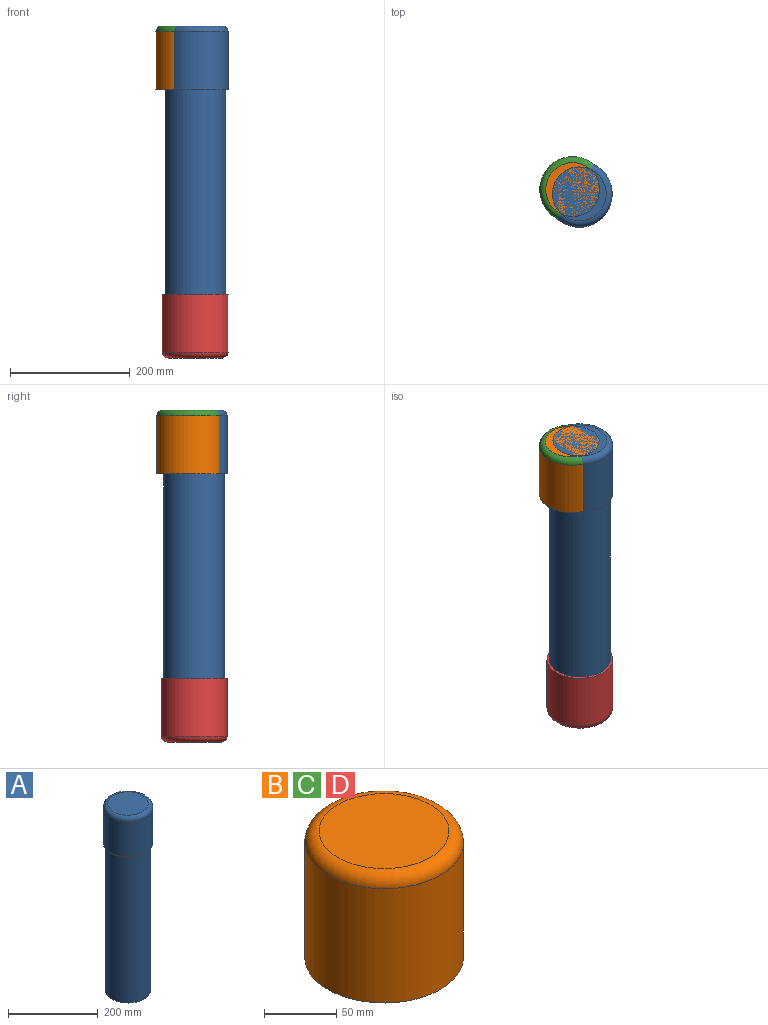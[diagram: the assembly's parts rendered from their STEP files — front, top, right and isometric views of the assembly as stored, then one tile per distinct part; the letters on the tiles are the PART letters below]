
ASSEMBLY  parts=4 mates=1
PART A: 8 faces, bbox 119.1x119.1x507 mm
  f0: cylinder r=46mm len=500mm, axis (0,0,1), area 144513.3mm2, adj f2,f3
  f1: cylinder r=51mm len=400mm, axis (0,0,1), area 128177mm2, adj f2,f4
  f2: plane 102x102mm, normal (0,0,-1), area 1523.7mm2, adj f0,f1
  f3: plane 92x92mm, normal (0,0,-1), area 6647.6mm2, adj f0
  f4: plane 110x110mm, normal (0,0,-1), area 1332mm2, adj f1,f6
  f5: plane 90x90mm, normal (0,0,1), area 6361.7mm2, adj f7
  f6: cylinder r=55mm len=110mm, axis (0,0,-1), area 33520.8mm2, adj f4,f7
  f7: torus R=45mm, axis (0,0,1), area 5069.6mm2, adj f5,f6
PART B: 8 faces, bbox 119.1x119.1x107 mm
  f0: cylinder r=46mm len=92mm, axis (0,0,1), area 14451.3mm2, adj f1,f2
  f1: plane 102x102mm, normal (0,0,-1), area 1523.7mm2, adj f0,f3
  f2: plane 92x92mm, normal (0,0,-1), area 6647.6mm2, adj f0
  f3: cylinder r=51mm len=102mm, axis (0,0,1), area 16022.1mm2, adj f1,f4
  f4: plane 110x110mm, normal (0,0,-1), area 1332mm2, adj f3,f6
  f5: plane 90x90mm, normal (0,0,1), area 6361.7mm2, adj f7
  f6: cylinder r=55mm len=110mm, axis (0,0,-1), area 33520.8mm2, adj f4,f7
  f7: torus R=45mm, axis (0,0,1), area 5069.6mm2, adj f5,f6
PART C: same geometry as B
PART D: same geometry as B
PLACE A t=(-185.36,-204.23,-79.05)mm
PLACE B t=(-196.37,-197.07,-79.05)mm
PLACE C t=(-196.37,-197.07,-79.05)mm
PLACE D rot(axis=(0,1,0),180deg) t=(-185.36,-204.23,-620.2)mm
MATE slider D.f0 <-> A.f0  axis (0,0,-1) through (-185.36,-204.23,-617.2)mm
